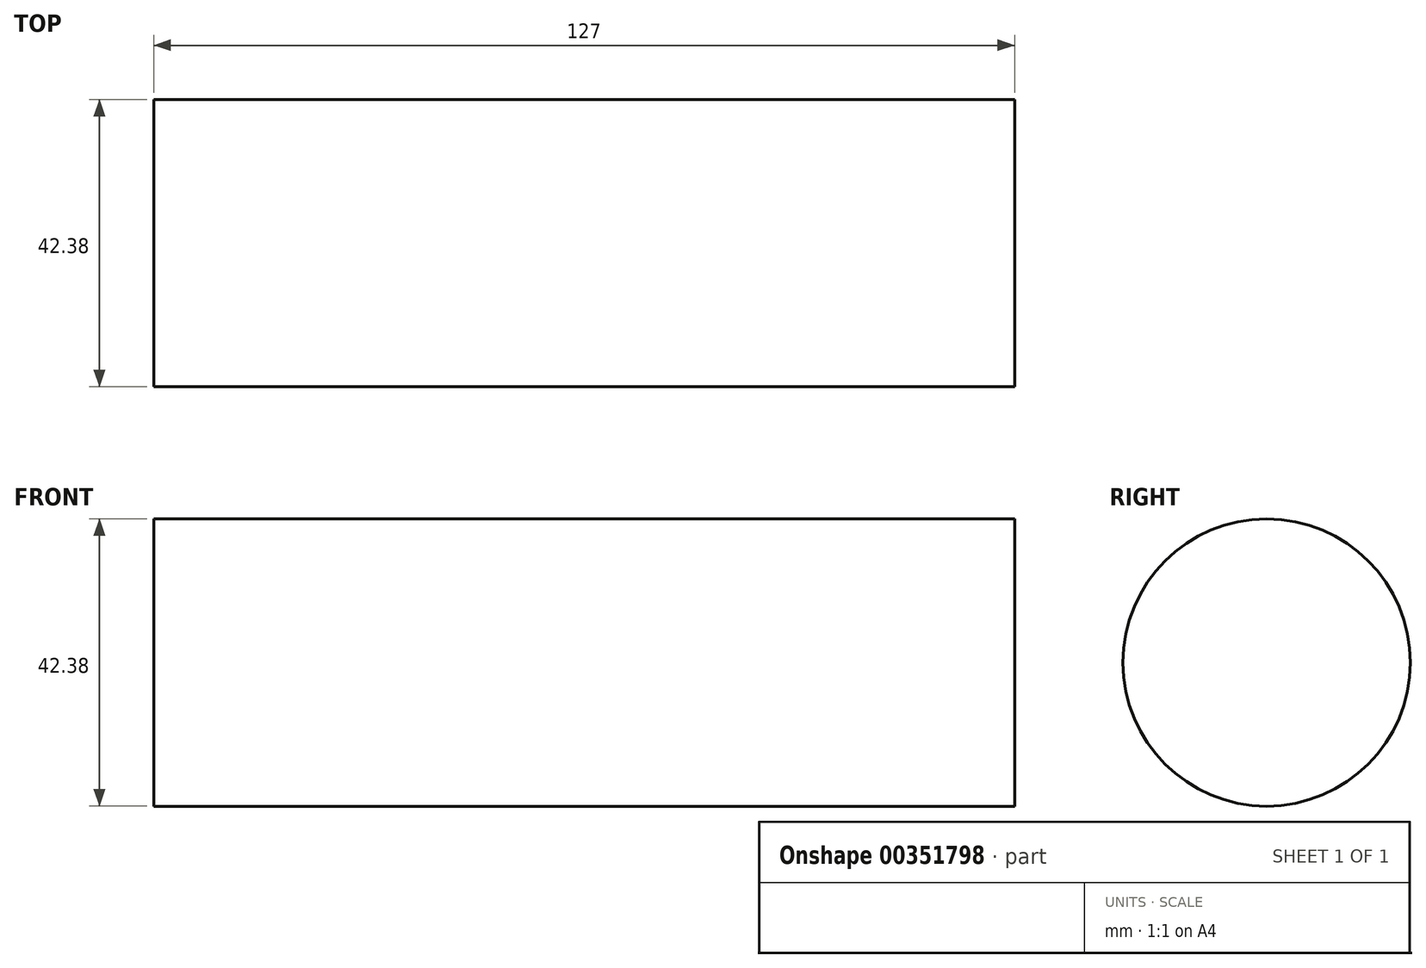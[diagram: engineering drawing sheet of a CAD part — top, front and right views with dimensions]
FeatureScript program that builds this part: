
annotation { "Feature Type Name" : "Feature", "Feature Type Description" : "" }
export const myFeature = defineFeature(function(context is Context, id is Id, definition is map)
    precondition{}
    {
        {
            var Q0;
            Q0=qCreatedBy(makeId("Right.planeOp"),FACE);
            var sketch = newSketch(context, id + "F0", { "sketchPlane" : qUnion([Q0])});
            skLineSegment(sketch, "E0", {"start": v(-36.1, 0) * mm, "end": v(0, 0) * mm});
            skCircle(sketch, "E1", {"center": v(0, 0) * mm, "radius": 21.2 * mm});
            skSolve(sketch);
        }
        {
            var Q0;
            Q0=makeQuery(id+"F0.imprint","IMPRINT",FACE,{"disambiguationData":[TD([[makeQuery(id+"F0.imprint","IMPRINT",EDGE,{"derivedFrom":sQuery(id+"F0.wireOp",EDGE,"E1")}),1.0]])]});
            extrude(context, id + "F1", {"entities" : qUnion([Q0]), "depth" : 127 * mm});
        }
    });
